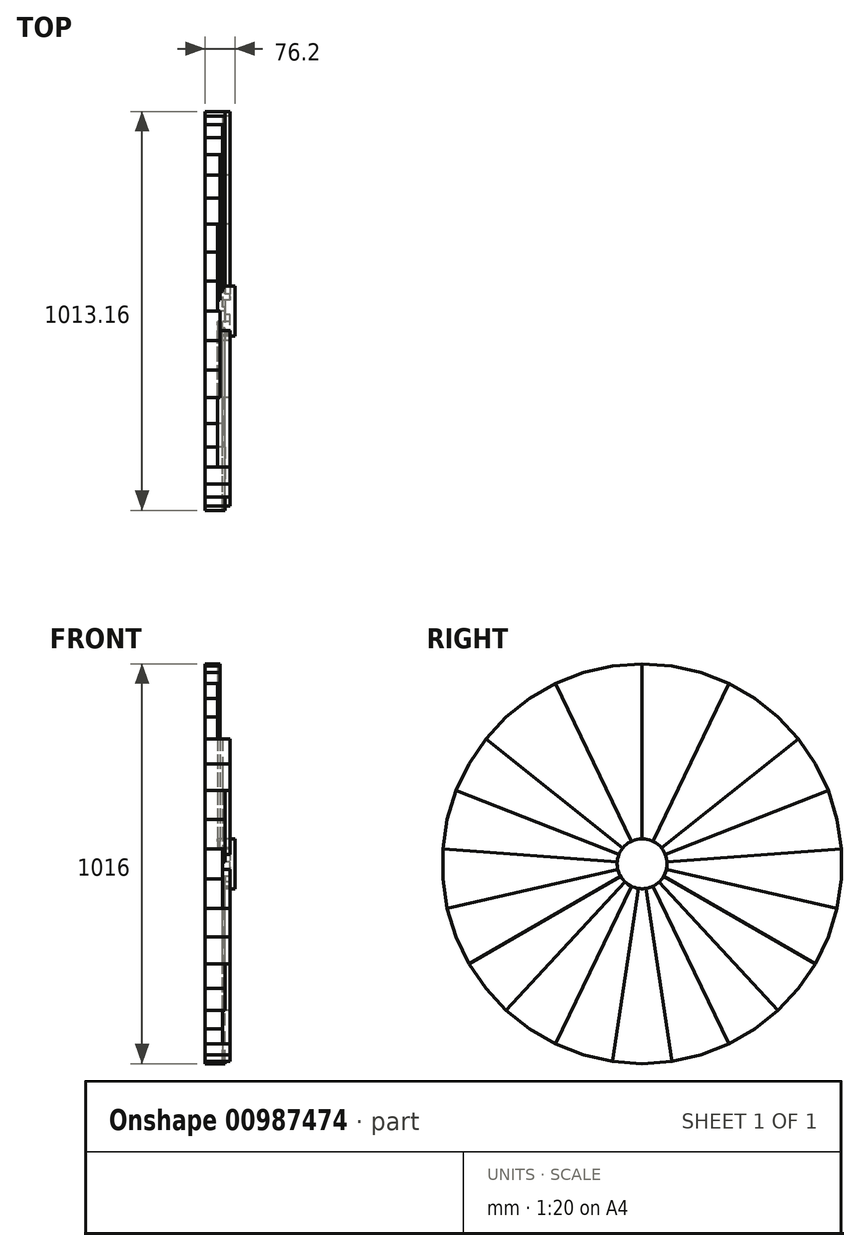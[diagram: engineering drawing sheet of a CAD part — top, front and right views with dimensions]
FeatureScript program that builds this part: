
annotation { "Feature Type Name" : "Feature", "Feature Type Description" : "" }
export const myFeature = defineFeature(function(context is Context, id is Id, definition is map)
    precondition{}
    {
        {
            var Q0;
            Q0=qCreatedBy(makeId("Right.planeOp"),FACE);
            var sketch = newSketch(context, id + "F0", { "sketchPlane" : qUnion([Q0])});
            skCircle(sketch, "E0", {"center": v(0, 0) * mm, "radius": 508 * mm});
            skCircle(sketch, "E1.cCircle", {"center": v(0, 0) * mm, "radius": 508 * mm, "construction": true});
            skLineSegment(sketch, "E1.0", {"start": v(-220.41, 457.7) * mm, "end": v(-149.74, 485.43) * mm});
            skLineSegment(sketch, "E1.1", {"start": v(-149.74, 485.43) * mm, "end": v(-75.71, 502.33) * mm});
            skLineSegment(sketch, "E1.2", {"start": v(-75.71, 502.33) * mm, "end": v(0, 508) * mm});
            skLineSegment(sketch, "E1.3", {"start": v(0, 508) * mm, "end": v(75.71, 502.33) * mm});
            skLineSegment(sketch, "E1.4", {"start": v(75.71, 502.33) * mm, "end": v(149.74, 485.43) * mm});
            skLineSegment(sketch, "E1.5", {"start": v(149.74, 485.43) * mm, "end": v(220.41, 457.7) * mm});
            skLineSegment(sketch, "E1.6", {"start": v(220.41, 457.7) * mm, "end": v(286.17, 419.73) * mm});
            skLineSegment(sketch, "E1.7", {"start": v(286.17, 419.73) * mm, "end": v(345.53, 372.4) * mm});
            skLineSegment(sketch, "E1.8", {"start": v(345.53, 372.4) * mm, "end": v(397.17, 316.73) * mm});
            skLineSegment(sketch, "E1.9", {"start": v(397.17, 316.73) * mm, "end": v(439.94, 254) * mm});
            skLineSegment(sketch, "E1.10", {"start": v(439.94, 254) * mm, "end": v(472.88, 185.6) * mm});
            skLineSegment(sketch, "E1.11", {"start": v(472.88, 185.6) * mm, "end": v(495.26, 113.04) * mm});
            skLineSegment(sketch, "E1.12", {"start": v(495.26, 113.04) * mm, "end": v(506.58, 37.96) * mm});
            skLineSegment(sketch, "E1.13", {"start": v(506.58, 37.96) * mm, "end": v(506.58, -37.96) * mm});
            skLineSegment(sketch, "E1.14", {"start": v(506.58, -37.96) * mm, "end": v(495.26, -113.04) * mm});
            skLineSegment(sketch, "E1.15", {"start": v(495.26, -113.04) * mm, "end": v(472.88, -185.6) * mm});
            skLineSegment(sketch, "E1.16", {"start": v(472.88, -185.6) * mm, "end": v(439.94, -254) * mm});
            skLineSegment(sketch, "E1.17", {"start": v(439.94, -254) * mm, "end": v(397.17, -316.73) * mm});
            skLineSegment(sketch, "E1.18", {"start": v(397.17, -316.73) * mm, "end": v(345.53, -372.4) * mm});
            skLineSegment(sketch, "E1.19", {"start": v(345.53, -372.4) * mm, "end": v(286.17, -419.73) * mm});
            skLineSegment(sketch, "E1.20", {"start": v(286.17, -419.73) * mm, "end": v(220.41, -457.7) * mm});
            skLineSegment(sketch, "E1.21", {"start": v(220.41, -457.7) * mm, "end": v(149.74, -485.43) * mm});
            skLineSegment(sketch, "E1.22", {"start": v(149.74, -485.43) * mm, "end": v(75.71, -502.33) * mm});
            skLineSegment(sketch, "E1.23", {"start": v(75.71, -502.33) * mm, "end": v(0, -508) * mm});
            skLineSegment(sketch, "E1.24", {"start": v(0, -508) * mm, "end": v(-75.71, -502.33) * mm});
            skLineSegment(sketch, "E1.25", {"start": v(-75.71, -502.33) * mm, "end": v(-149.74, -485.43) * mm});
            skLineSegment(sketch, "E1.26", {"start": v(-149.74, -485.43) * mm, "end": v(-220.41, -457.7) * mm});
            skLineSegment(sketch, "E1.27", {"start": v(-220.41, -457.7) * mm, "end": v(-286.17, -419.73) * mm});
            skLineSegment(sketch, "E1.28", {"start": v(-286.17, -419.73) * mm, "end": v(-345.53, -372.4) * mm});
            skLineSegment(sketch, "E1.29", {"start": v(-345.53, -372.4) * mm, "end": v(-397.17, -316.73) * mm});
            skLineSegment(sketch, "E1.30", {"start": v(-397.17, -316.73) * mm, "end": v(-439.94, -254) * mm});
            skLineSegment(sketch, "E1.31", {"start": v(-439.94, -254) * mm, "end": v(-472.88, -185.6) * mm});
            skLineSegment(sketch, "E1.32", {"start": v(-472.88, -185.6) * mm, "end": v(-495.26, -113.04) * mm});
            skLineSegment(sketch, "E1.33", {"start": v(-495.26, -113.04) * mm, "end": v(-506.58, -37.96) * mm});
            skLineSegment(sketch, "E1.34", {"start": v(-506.58, -37.96) * mm, "end": v(-506.58, 37.96) * mm});
            skLineSegment(sketch, "E1.35", {"start": v(-506.58, 37.96) * mm, "end": v(-495.26, 113.04) * mm});
            skLineSegment(sketch, "E1.36", {"start": v(-495.26, 113.04) * mm, "end": v(-472.88, 185.6) * mm});
            skLineSegment(sketch, "E1.37", {"start": v(-472.88, 185.6) * mm, "end": v(-439.94, 254) * mm});
            skLineSegment(sketch, "E1.38", {"start": v(-439.94, 254) * mm, "end": v(-397.17, 316.73) * mm});
            skLineSegment(sketch, "E1.39", {"start": v(-397.17, 316.73) * mm, "end": v(-345.53, 372.4) * mm});
            skLineSegment(sketch, "E1.40", {"start": v(-345.53, 372.4) * mm, "end": v(-286.17, 419.73) * mm});
            skLineSegment(sketch, "E1.41", {"start": v(-286.17, 419.73) * mm, "end": v(-220.41, 457.7) * mm});
            skLineSegment(sketch, "E2", {"start": v(0, 508) * mm, "end": v(0, 0) * mm});
            skLineSegment(sketch, "E3", {"start": v(220.41, 457.7) * mm, "end": v(0, 0) * mm});
            skLineSegment(sketch, "E4", {"start": v(397.17, 316.73) * mm, "end": v(0, 0) * mm});
            skLineSegment(sketch, "E5", {"start": v(-220.41, 457.7) * mm, "end": v(0, 0) * mm});
            skLineSegment(sketch, "E6", {"start": v(-397.17, 316.73) * mm, "end": v(0, 0) * mm});
            skLineSegment(sketch, "E7", {"start": v(472.88, 185.6) * mm, "end": v(0, 0) * mm});
            skLineSegment(sketch, "E8", {"start": v(506.58, 37.96) * mm, "end": v(0, 0) * mm});
            skLineSegment(sketch, "E9", {"start": v(495.26, -113.04) * mm, "end": v(0, 0) * mm});
            skLineSegment(sketch, "E10", {"start": v(439.94, -254) * mm, "end": v(0, 0) * mm});
            skLineSegment(sketch, "E11", {"start": v(345.53, -372.4) * mm, "end": v(0, 0) * mm});
            skLineSegment(sketch, "E12", {"start": v(220.41, -457.7) * mm, "end": v(0, 0) * mm});
            skLineSegment(sketch, "E13", {"start": v(75.71, -502.33) * mm, "end": v(0, 0) * mm});
            skLineSegment(sketch, "E14", {"start": v(-75.71, -502.33) * mm, "end": v(0, 0) * mm});
            skLineSegment(sketch, "E15", {"start": v(-220.41, -457.7) * mm, "end": v(0, 0) * mm});
            skLineSegment(sketch, "E16", {"start": v(-345.53, -372.4) * mm, "end": v(0, 0) * mm});
            skLineSegment(sketch, "E17", {"start": v(-439.94, -254) * mm, "end": v(0, 0) * mm});
            skLineSegment(sketch, "E18", {"start": v(-495.26, -113.04) * mm, "end": v(0, 0) * mm});
            skLineSegment(sketch, "E19", {"start": v(-506.58, 37.96) * mm, "end": v(0, 0) * mm});
            skLineSegment(sketch, "E20", {"start": v(-472.88, 185.6) * mm, "end": v(0, 0) * mm});
            skCircle(sketch, "E21", {"center": v(1271.03, -28.32) * mm, "radius": 508 * mm});
            skCircle(sketch, "E22", {"center": v(-1617.24, 20.06) * mm, "radius": 508 * mm});
            skCircle(sketch, "E23.cCircle", {"center": v(-1617.24, 20.06) * mm, "radius": 508 * mm, "construction": true});
            skLineSegment(sketch, "E23.0", {"start": v(-1897.2, 443.96) * mm, "end": v(-1830.9, 480.95) * mm});
            skLineSegment(sketch, "E23.1", {"start": v(-1830.9, 480.95) * mm, "end": v(-1759.81, 507.65) * mm});
            skLineSegment(sketch, "E23.2", {"start": v(-1759.81, 507.65) * mm, "end": v(-1685.55, 523.45) * mm});
            skLineSegment(sketch, "E23.3", {"start": v(-1685.55, 523.45) * mm, "end": v(-1609.76, 528) * mm});
            skLineSegment(sketch, "E23.4", {"start": v(-1609.76, 528) * mm, "end": v(-1534.14, 521.22) * mm});
            skLineSegment(sketch, "E23.5", {"start": v(-1534.14, 521.22) * mm, "end": v(-1460.37, 503.23) * mm});
            skLineSegment(sketch, "E23.6", {"start": v(-1460.37, 503.23) * mm, "end": v(-1390.11, 474.46) * mm});
            skLineSegment(sketch, "E23.7", {"start": v(-1390.11, 474.46) * mm, "end": v(-1324.93, 435.53) * mm});
            skLineSegment(sketch, "E23.8", {"start": v(-1324.93, 435.53) * mm, "end": v(-1266.27, 387.32) * mm});
            skLineSegment(sketch, "E23.9", {"start": v(-1266.27, 387.32) * mm, "end": v(-1215.45, 330.9) * mm});
            skLineSegment(sketch, "E23.10", {"start": v(-1215.45, 330.9) * mm, "end": v(-1173.6, 267.55) * mm});
            skLineSegment(sketch, "E23.11", {"start": v(-1173.6, 267.55) * mm, "end": v(-1141.68, 198.67) * mm});
            skLineSegment(sketch, "E23.12", {"start": v(-1141.68, 198.67) * mm, "end": v(-1120.37, 125.8) * mm});
            skLineSegment(sketch, "E23.13", {"start": v(-1120.37, 125.8) * mm, "end": v(-1110.16, 50.56) * mm});
            skLineSegment(sketch, "E23.14", {"start": v(-1110.16, 50.56) * mm, "end": v(-1111.28, -25.36) * mm});
            skLineSegment(sketch, "E23.15", {"start": v(-1111.28, -25.36) * mm, "end": v(-1123.7, -100.26) * mm});
            skLineSegment(sketch, "E23.16", {"start": v(-1123.7, -100.26) * mm, "end": v(-1147.15, -172.48) * mm});
            skLineSegment(sketch, "E23.17", {"start": v(-1147.15, -172.48) * mm, "end": v(-1181.1, -240.4) * mm});
            skLineSegment(sketch, "E23.18", {"start": v(-1181.1, -240.4) * mm, "end": v(-1224.78, -302.49) * mm});
            skLineSegment(sketch, "E23.19", {"start": v(-1224.78, -302.49) * mm, "end": v(-1277.24, -357.38) * mm});
            skLineSegment(sketch, "E23.20", {"start": v(-1277.24, -357.38) * mm, "end": v(-1337.3, -403.84) * mm});
            skLineSegment(sketch, "E23.21", {"start": v(-1337.3, -403.84) * mm, "end": v(-1403.6, -440.83) * mm});
            skLineSegment(sketch, "E23.22", {"start": v(-1403.6, -440.83) * mm, "end": v(-1474.68, -467.52) * mm});
            skLineSegment(sketch, "E23.23", {"start": v(-1474.68, -467.52) * mm, "end": v(-1548.94, -483.33) * mm});
            skLineSegment(sketch, "E23.24", {"start": v(-1548.94, -483.33) * mm, "end": v(-1624.73, -487.88) * mm});
            skLineSegment(sketch, "E23.25", {"start": v(-1624.73, -487.88) * mm, "end": v(-1700.35, -481.1) * mm});
            skLineSegment(sketch, "E23.26", {"start": v(-1700.35, -481.1) * mm, "end": v(-1774.11, -463.11) * mm});
            skLineSegment(sketch, "E23.27", {"start": v(-1774.11, -463.11) * mm, "end": v(-1844.38, -434.33) * mm});
            skLineSegment(sketch, "E23.28", {"start": v(-1844.38, -434.33) * mm, "end": v(-1909.56, -395.4) * mm});
            skLineSegment(sketch, "E23.29", {"start": v(-1909.56, -395.4) * mm, "end": v(-1968.22, -347.2) * mm});
            skLineSegment(sketch, "E23.30", {"start": v(-1968.22, -347.2) * mm, "end": v(-2019.04, -290.79) * mm});
            skLineSegment(sketch, "E23.31", {"start": v(-2019.04, -290.79) * mm, "end": v(-2060.88, -227.43) * mm});
            skLineSegment(sketch, "E23.32", {"start": v(-2060.88, -227.43) * mm, "end": v(-2092.81, -158.55) * mm});
            skLineSegment(sketch, "E23.33", {"start": v(-2092.81, -158.55) * mm, "end": v(-2114.12, -85.67) * mm});
            skLineSegment(sketch, "E23.34", {"start": v(-2114.12, -85.67) * mm, "end": v(-2124.33, -10.43) * mm});
            skLineSegment(sketch, "E23.35", {"start": v(-2124.33, -10.43) * mm, "end": v(-2123.2, 65.48) * mm});
            skLineSegment(sketch, "E23.36", {"start": v(-2123.2, 65.48) * mm, "end": v(-2110.79, 140.39) * mm});
            skLineSegment(sketch, "E23.37", {"start": v(-2110.79, 140.39) * mm, "end": v(-2087.34, 212.6) * mm});
            skLineSegment(sketch, "E23.38", {"start": v(-2087.34, 212.6) * mm, "end": v(-2053.4, 280.51) * mm});
            skLineSegment(sketch, "E23.39", {"start": v(-2053.4, 280.51) * mm, "end": v(-2009.7, 342.61) * mm});
            skLineSegment(sketch, "E23.40", {"start": v(-2009.7, 342.61) * mm, "end": v(-1957.25, 397.5) * mm});
            skLineSegment(sketch, "E23.41", {"start": v(-1957.25, 397.5) * mm, "end": v(-1897.2, 443.96) * mm});
            skLineSegment(sketch, "E24", {"start": v(-1685.55, 523.45) * mm, "end": v(-1617.24, 20.06) * mm});
            skLineSegment(sketch, "E25", {"start": v(-1460.37, 503.23) * mm, "end": v(-1617.24, 20.06) * mm});
            skLineSegment(sketch, "E26", {"start": v(-1266.27, 387.32) * mm, "end": v(-1617.24, 20.06) * mm});
            skLineSegment(sketch, "E27", {"start": v(-1897.2, 443.96) * mm, "end": v(-1617.24, 20.06) * mm});
            skLineSegment(sketch, "E28", {"start": v(-2053.4, 280.51) * mm, "end": v(-1617.24, 20.06) * mm});
            skLineSegment(sketch, "E29", {"start": v(-1173.6, 267.55) * mm, "end": v(-1617.24, 20.06) * mm});
            skLineSegment(sketch, "E30", {"start": v(-1120.37, 125.8) * mm, "end": v(-1617.24, 20.06) * mm});
            skLineSegment(sketch, "E31", {"start": v(-1111.28, -25.36) * mm, "end": v(-1617.24, 20.06) * mm});
            skLineSegment(sketch, "E32", {"start": v(-1147.15, -172.48) * mm, "end": v(-1617.24, 20.06) * mm});
            skLineSegment(sketch, "E33", {"start": v(-1224.78, -302.49) * mm, "end": v(-1617.24, 20.06) * mm});
            skLineSegment(sketch, "E34", {"start": v(-1337.3, -403.84) * mm, "end": v(-1617.24, 20.06) * mm});
            skLineSegment(sketch, "E35", {"start": v(-1474.68, -467.52) * mm, "end": v(-1617.24, 20.06) * mm});
            skLineSegment(sketch, "E36", {"start": v(-1624.73, -487.88) * mm, "end": v(-1617.24, 20.06) * mm});
            skLineSegment(sketch, "E37", {"start": v(-1774.11, -463.11) * mm, "end": v(-1617.24, 20.06) * mm});
            skLineSegment(sketch, "E38", {"start": v(-1909.56, -395.4) * mm, "end": v(-1617.24, 20.06) * mm});
            skLineSegment(sketch, "E39", {"start": v(-2019.04, -290.79) * mm, "end": v(-1617.24, 20.06) * mm});
            skLineSegment(sketch, "E40", {"start": v(-2092.81, -158.55) * mm, "end": v(-1617.24, 20.06) * mm});
            skLineSegment(sketch, "E41", {"start": v(-2124.33, -10.43) * mm, "end": v(-1617.24, 20.06) * mm});
            skLineSegment(sketch, "E42", {"start": v(-2110.79, 140.39) * mm, "end": v(-1617.24, 20.06) * mm});
            skCircle(sketch, "E43", {"center": v(0, 0) * mm, "radius": 63.5 * mm});
            skSolve(sketch);
        }
        {
            var Q0;
            Q0=makeQuery(id+"F0.imprint","IMPRINT",FACE,{"disambiguationData":[TD([[makeQuery(id+"F0.imprint","IMPRINT",EDGE,{"derivedFrom":sQuery(id+"F0.wireOp",EDGE,"E1.0")}),-1.0]])]});
            var Q1;
            Q1=makeQuery(id+"F0.imprint","IMPRINT",FACE,{"disambiguationData":[TD([[makeQuery(id+"F0.imprint","IMPRINT",EDGE,{"derivedFrom":sQuery(id+"F0.wireOp",EDGE,"E1.3")}),-1.0]])]});
            var Q2;
            Q2=makeQuery(id+"F0.imprint","IMPRINT",FACE,{"disambiguationData":[TD([[makeQuery(id+"F0.imprint","IMPRINT",EDGE,{"derivedFrom":sQuery(id+"F0.wireOp",EDGE,"E1.6")}),-1.0]])]});
            var Q3;
            Q3=makeQuery(id+"F0.imprint","IMPRINT",FACE,{"disambiguationData":[TD([[makeQuery(id+"F0.imprint","IMPRINT",EDGE,{"derivedFrom":sQuery(id+"F0.wireOp",EDGE,"E1.9")}),-1.0]])]});
            var Q4;
            Q4=makeQuery(id+"F0.imprint","IMPRINT",FACE,{"disambiguationData":[TD([[makeQuery(id+"F0.imprint","IMPRINT",EDGE,{"derivedFrom":sQuery(id+"F0.wireOp",EDGE,"E1.11")}),-1.0]])]});
            var Q5;
            Q5=makeQuery(id+"F0.imprint","IMPRINT",FACE,{"disambiguationData":[TD([[makeQuery(id+"F0.imprint","IMPRINT",EDGE,{"derivedFrom":sQuery(id+"F0.wireOp",EDGE,"E1.13")}),-1.0]])]});
            var Q6;
            Q6=makeQuery(id+"F0.imprint","IMPRINT",FACE,{"disambiguationData":[TD([[makeQuery(id+"F0.imprint","IMPRINT",EDGE,{"derivedFrom":sQuery(id+"F0.wireOp",EDGE,"E1.15")}),-1.0]])]});
            var Q7;
            Q7=makeQuery(id+"F0.imprint","IMPRINT",FACE,{"disambiguationData":[TD([[makeQuery(id+"F0.imprint","IMPRINT",EDGE,{"derivedFrom":sQuery(id+"F0.wireOp",EDGE,"E1.17")}),-1.0]])]});
            var Q8;
            Q8=makeQuery(id+"F0.imprint","IMPRINT",FACE,{"disambiguationData":[TD([[makeQuery(id+"F0.imprint","IMPRINT",EDGE,{"derivedFrom":sQuery(id+"F0.wireOp",EDGE,"E1.19")}),-1.0]])]});
            var Q9;
            Q9=makeQuery(id+"F0.imprint","IMPRINT",FACE,{"disambiguationData":[TD([[makeQuery(id+"F0.imprint","IMPRINT",EDGE,{"derivedFrom":sQuery(id+"F0.wireOp",EDGE,"E1.21")}),-1.0]])]});
            var Q10;
            Q10=makeQuery(id+"F0.imprint","IMPRINT",FACE,{"disambiguationData":[TD([[makeQuery(id+"F0.imprint","IMPRINT",EDGE,{"derivedFrom":sQuery(id+"F0.wireOp",EDGE,"E1.23")}),-1.0]])]});
            var Q11;
            Q11=makeQuery(id+"F0.imprint","IMPRINT",FACE,{"disambiguationData":[TD([[makeQuery(id+"F0.imprint","IMPRINT",EDGE,{"derivedFrom":sQuery(id+"F0.wireOp",EDGE,"E1.25")}),-1.0]])]});
            var Q12;
            Q12=makeQuery(id+"F0.imprint","IMPRINT",FACE,{"disambiguationData":[TD([[makeQuery(id+"F0.imprint","IMPRINT",EDGE,{"derivedFrom":sQuery(id+"F0.wireOp",EDGE,"E1.27")}),-1.0]])]});
            var Q13;
            Q13=makeQuery(id+"F0.imprint","IMPRINT",FACE,{"disambiguationData":[TD([[makeQuery(id+"F0.imprint","IMPRINT",EDGE,{"derivedFrom":sQuery(id+"F0.wireOp",EDGE,"E1.29")}),-1.0]])]});
            var Q14;
            Q14=makeQuery(id+"F0.imprint","IMPRINT",FACE,{"disambiguationData":[TD([[makeQuery(id+"F0.imprint","IMPRINT",EDGE,{"derivedFrom":sQuery(id+"F0.wireOp",EDGE,"E1.31")}),-1.0]])]});
            var Q15;
            Q15=makeQuery(id+"F0.imprint","IMPRINT",FACE,{"disambiguationData":[TD([[makeQuery(id+"F0.imprint","IMPRINT",EDGE,{"derivedFrom":sQuery(id+"F0.wireOp",EDGE,"E1.33")}),-1.0]])]});
            var Q16;
            Q16=makeQuery(id+"F0.imprint","IMPRINT",FACE,{"disambiguationData":[TD([[makeQuery(id+"F0.imprint","IMPRINT",EDGE,{"derivedFrom":sQuery(id+"F0.wireOp",EDGE,"E1.35")}),-1.0]])]});
            var Q17;
            Q17=makeQuery(id+"F0.imprint","IMPRINT",FACE,{"disambiguationData":[TD([[makeQuery(id+"F0.imprint","IMPRINT",EDGE,{"derivedFrom":sQuery(id+"F0.wireOp",EDGE,"E1.37")}),-1.0]])]});
            var Q18;
            Q18=makeQuery(id+"F0.imprint","IMPRINT",FACE,{"disambiguationData":[TD([[makeQuery(id+"F0.imprint","IMPRINT",EDGE,{"derivedFrom":sQuery(id+"F0.wireOp",EDGE,"E1.39")}),-1.0]])]});
            extrude(context, id + "F1", {"entities" : qUnion([Q0, Q1, Q2, Q3, Q4, Q5, Q6, Q7, Q8, Q9, Q10, Q11, Q12, Q13, Q14, Q15, Q16, Q17, Q18]), "depth" : 25.4 * mm, "offsetDistance" : 25.4 * mm});
        }
        {
            var Q0;
            {var subQ1=sQuery(id+"F0.wireOp",EDGE,"E1.3");Q0=makeQuery(id+"F0.imprint","IMPRINT",FACE,{"disambiguationData":[TD([[makeQuery(id+"F0.imprint","IMPRINT",EDGE,{"derivedFrom":subQ1}),-1.0]])]});}
            var Q1;
            {var subQ5=sQuery(id+"F0.wireOp",EDGE,"E1.39");Q1=makeQuery(id+"F0.imprint","IMPRINT",FACE,{"disambiguationData":[TD([[makeQuery(id+"F0.imprint","IMPRINT",EDGE,{"derivedFrom":subQ5}),-1.0]])]});}
            var Q2;
            {var subQ1=sQuery(id+"F0.wireOp",EDGE,"E2");var subQ3=sQuery(id+"F0.wireOp",EDGE,"E43");var subQ4=makeQuery(id+"F0.imprint","INTERSECT",VERTEX,{"derivedFrom":[subQ1,subQ3]});Q2=makeQuery(id+"F0.imprint","IMPRINT",FACE,{"disambiguationData":[TD([[makeQuery(id+"F0.imprint","IMPRINT",EDGE,{"disambiguationData":[TD([[subQ4,1.0]])],"derivedFrom":subQ3}),1.0]])]});}
            var Q3;
            {var subQ1=sQuery(id+"F0.wireOp",EDGE,"E2");var subQ3=sQuery(id+"F0.wireOp",EDGE,"E43");var subQ4=makeQuery(id+"F0.imprint","INTERSECT",VERTEX,{"derivedFrom":[subQ1,subQ3]});Q3=makeQuery(id+"F0.imprint","IMPRINT",FACE,{"disambiguationData":[TD([[makeQuery(id+"F0.imprint","IMPRINT",EDGE,{"disambiguationData":[TD([[subQ4,-1.0]])],"derivedFrom":subQ3}),1.0]])]});}
            var Q4;
            {var subQ1=sQuery(id+"F0.wireOp",EDGE,"E5");var subQ3=sQuery(id+"F0.wireOp",EDGE,"E43");var subQ4=makeQuery(id+"F0.imprint","INTERSECT",VERTEX,{"derivedFrom":[subQ1,subQ3]});Q4=makeQuery(id+"F0.imprint","IMPRINT",FACE,{"disambiguationData":[TD([[makeQuery(id+"F0.imprint","IMPRINT",EDGE,{"disambiguationData":[TD([[subQ4,-1.0]])],"derivedFrom":subQ3}),1.0]])]});}
            extrude(context, id + "F2", {"entities" : qUnion([Q0, Q1, Q2, Q3, Q4]), "operationType" : NewBodyOperationType.ADD, "depth" : 31.75 * mm, "offsetDistance" : 25.4 * mm});
        }
        {
            var Q0;
            {var subQ7=sQuery(id+"F0.wireOp",EDGE,"E1.0");Q0=makeQuery(id+"F0.imprint","IMPRINT",FACE,{"disambiguationData":[TD([[makeQuery(id+"F0.imprint","IMPRINT",EDGE,{"derivedFrom":subQ7}),-1.0]])]});}
            var Q1;
            {var subQ1=sQuery(id+"F0.wireOp",EDGE,"E1.6");Q1=makeQuery(id+"F0.imprint","IMPRINT",FACE,{"disambiguationData":[TD([[makeQuery(id+"F0.imprint","IMPRINT",EDGE,{"derivedFrom":subQ1}),-1.0]])]});}
            var Q2;
            {var subQ1=sQuery(id+"F0.wireOp",EDGE,"E3");var subQ3=sQuery(id+"F0.wireOp",EDGE,"E43");var subQ4=makeQuery(id+"F0.imprint","INTERSECT",VERTEX,{"derivedFrom":[subQ1,subQ3]});Q2=makeQuery(id+"F0.imprint","IMPRINT",FACE,{"disambiguationData":[TD([[makeQuery(id+"F0.imprint","IMPRINT",EDGE,{"disambiguationData":[TD([[subQ4,1.0]])],"derivedFrom":subQ3}),1.0]])]});}
            var Q3;
            {var subQ1=sQuery(id+"F0.wireOp",EDGE,"E2");var subQ3=sQuery(id+"F0.wireOp",EDGE,"E43");var subQ4=makeQuery(id+"F0.imprint","INTERSECT",VERTEX,{"derivedFrom":[subQ1,subQ3]});Q3=makeQuery(id+"F0.imprint","IMPRINT",FACE,{"disambiguationData":[TD([[makeQuery(id+"F0.imprint","IMPRINT",EDGE,{"disambiguationData":[TD([[subQ4,1.0]])],"derivedFrom":subQ3}),1.0]])]});}
            var Q4;
            {var subQ1=sQuery(id+"F0.wireOp",EDGE,"E2");var subQ3=sQuery(id+"F0.wireOp",EDGE,"E43");var subQ4=makeQuery(id+"F0.imprint","INTERSECT",VERTEX,{"derivedFrom":[subQ1,subQ3]});Q4=makeQuery(id+"F0.imprint","IMPRINT",FACE,{"disambiguationData":[TD([[makeQuery(id+"F0.imprint","IMPRINT",EDGE,{"disambiguationData":[TD([[subQ4,-1.0]])],"derivedFrom":subQ3}),1.0]])]});}
            extrude(context, id + "F3", {"entities" : qUnion([Q0, Q1, Q2, Q3, Q4]), "operationType" : NewBodyOperationType.ADD, "depth" : 38.1 * mm, "offsetDistance" : 25.4 * mm});
        }
        {
            var Q0;
            {var subQ6=sQuery(id+"F0.wireOp",EDGE,"E1.9");Q0=makeQuery(id+"F0.imprint","IMPRINT",FACE,{"disambiguationData":[TD([[makeQuery(id+"F0.imprint","IMPRINT",EDGE,{"derivedFrom":subQ6}),-1.0]])]});}
            var Q1;
            {var subQ7=sQuery(id+"F0.wireOp",EDGE,"E1.15");Q1=makeQuery(id+"F0.imprint","IMPRINT",FACE,{"disambiguationData":[TD([[makeQuery(id+"F0.imprint","IMPRINT",EDGE,{"derivedFrom":subQ7}),-1.0]])]});}
            var Q2;
            {var subQ6=sQuery(id+"F0.wireOp",EDGE,"E1.21");Q2=makeQuery(id+"F0.imprint","IMPRINT",FACE,{"disambiguationData":[TD([[makeQuery(id+"F0.imprint","IMPRINT",EDGE,{"derivedFrom":subQ6}),-1.0]])]});}
            var Q3;
            {var subQ6=sQuery(id+"F0.wireOp",EDGE,"E1.27");Q3=makeQuery(id+"F0.imprint","IMPRINT",FACE,{"disambiguationData":[TD([[makeQuery(id+"F0.imprint","IMPRINT",EDGE,{"derivedFrom":subQ6}),-1.0]])]});}
            var Q4;
            {var subQ6=sQuery(id+"F0.wireOp",EDGE,"E1.33");Q4=makeQuery(id+"F0.imprint","IMPRINT",FACE,{"disambiguationData":[TD([[makeQuery(id+"F0.imprint","IMPRINT",EDGE,{"derivedFrom":subQ6}),-1.0]])]});}
            var Q5;
            {var subQ1=sQuery(id+"F0.wireOp",EDGE,"E4");var subQ3=sQuery(id+"F0.wireOp",EDGE,"E43");var subQ4=makeQuery(id+"F0.imprint","INTERSECT",VERTEX,{"derivedFrom":[subQ1,subQ3]});Q5=makeQuery(id+"F0.imprint","IMPRINT",FACE,{"disambiguationData":[TD([[makeQuery(id+"F0.imprint","IMPRINT",EDGE,{"disambiguationData":[TD([[subQ4,1.0]])],"derivedFrom":subQ3}),1.0]])]});}
            var Q6;
            {var subQ1=sQuery(id+"F0.wireOp",EDGE,"E7");var subQ3=sQuery(id+"F0.wireOp",EDGE,"E43");var subQ4=makeQuery(id+"F0.imprint","INTERSECT",VERTEX,{"derivedFrom":[subQ1,subQ3]});Q6=makeQuery(id+"F0.imprint","IMPRINT",FACE,{"disambiguationData":[TD([[makeQuery(id+"F0.imprint","IMPRINT",EDGE,{"disambiguationData":[TD([[subQ4,1.0]])],"derivedFrom":subQ3}),1.0]])]});}
            var Q7;
            {var subQ1=sQuery(id+"F0.wireOp",EDGE,"E8");var subQ3=sQuery(id+"F0.wireOp",EDGE,"E43");var subQ4=makeQuery(id+"F0.imprint","INTERSECT",VERTEX,{"derivedFrom":[subQ1,subQ3]});Q7=makeQuery(id+"F0.imprint","IMPRINT",FACE,{"disambiguationData":[TD([[makeQuery(id+"F0.imprint","IMPRINT",EDGE,{"disambiguationData":[TD([[subQ4,1.0]])],"derivedFrom":subQ3}),1.0]])]});}
            var Q8;
            {var subQ1=sQuery(id+"F0.wireOp",EDGE,"E9");var subQ3=sQuery(id+"F0.wireOp",EDGE,"E43");var subQ4=makeQuery(id+"F0.imprint","INTERSECT",VERTEX,{"derivedFrom":[subQ1,subQ3]});Q8=makeQuery(id+"F0.imprint","IMPRINT",FACE,{"disambiguationData":[TD([[makeQuery(id+"F0.imprint","IMPRINT",EDGE,{"disambiguationData":[TD([[subQ4,1.0]])],"derivedFrom":subQ3}),1.0]])]});}
            var Q9;
            {var subQ1=sQuery(id+"F0.wireOp",EDGE,"E10");var subQ3=sQuery(id+"F0.wireOp",EDGE,"E43");var subQ4=makeQuery(id+"F0.imprint","INTERSECT",VERTEX,{"derivedFrom":[subQ1,subQ3]});Q9=makeQuery(id+"F0.imprint","IMPRINT",FACE,{"disambiguationData":[TD([[makeQuery(id+"F0.imprint","IMPRINT",EDGE,{"disambiguationData":[TD([[subQ4,1.0]])],"derivedFrom":subQ3}),1.0]])]});}
            var Q10;
            {var subQ1=sQuery(id+"F0.wireOp",EDGE,"E11");var subQ3=sQuery(id+"F0.wireOp",EDGE,"E43");var subQ4=makeQuery(id+"F0.imprint","INTERSECT",VERTEX,{"derivedFrom":[subQ1,subQ3]});Q10=makeQuery(id+"F0.imprint","IMPRINT",FACE,{"disambiguationData":[TD([[makeQuery(id+"F0.imprint","IMPRINT",EDGE,{"disambiguationData":[TD([[subQ4,1.0]])],"derivedFrom":subQ3}),1.0]])]});}
            var Q11;
            {var subQ1=sQuery(id+"F0.wireOp",EDGE,"E12");var subQ3=sQuery(id+"F0.wireOp",EDGE,"E43");var subQ4=makeQuery(id+"F0.imprint","INTERSECT",VERTEX,{"derivedFrom":[subQ1,subQ3]});Q11=makeQuery(id+"F0.imprint","IMPRINT",FACE,{"disambiguationData":[TD([[makeQuery(id+"F0.imprint","IMPRINT",EDGE,{"disambiguationData":[TD([[subQ4,1.0]])],"derivedFrom":subQ3}),1.0]])]});}
            var Q12;
            {var subQ1=sQuery(id+"F0.wireOp",EDGE,"E13");var subQ3=sQuery(id+"F0.wireOp",EDGE,"E43");var subQ4=makeQuery(id+"F0.imprint","INTERSECT",VERTEX,{"derivedFrom":[subQ1,subQ3]});Q12=makeQuery(id+"F0.imprint","IMPRINT",FACE,{"disambiguationData":[TD([[makeQuery(id+"F0.imprint","IMPRINT",EDGE,{"disambiguationData":[TD([[subQ4,1.0]])],"derivedFrom":subQ3}),1.0]])]});}
            var Q13;
            {var subQ1=sQuery(id+"F0.wireOp",EDGE,"E14");var subQ3=sQuery(id+"F0.wireOp",EDGE,"E43");var subQ4=makeQuery(id+"F0.imprint","INTERSECT",VERTEX,{"derivedFrom":[subQ1,subQ3]});Q13=makeQuery(id+"F0.imprint","IMPRINT",FACE,{"disambiguationData":[TD([[makeQuery(id+"F0.imprint","IMPRINT",EDGE,{"disambiguationData":[TD([[subQ4,1.0]])],"derivedFrom":subQ3}),1.0]])]});}
            var Q14;
            {var subQ1=sQuery(id+"F0.wireOp",EDGE,"E15");var subQ3=sQuery(id+"F0.wireOp",EDGE,"E43");var subQ4=makeQuery(id+"F0.imprint","INTERSECT",VERTEX,{"derivedFrom":[subQ1,subQ3]});Q14=makeQuery(id+"F0.imprint","IMPRINT",FACE,{"disambiguationData":[TD([[makeQuery(id+"F0.imprint","IMPRINT",EDGE,{"disambiguationData":[TD([[subQ4,1.0]])],"derivedFrom":subQ3}),1.0]])]});}
            var Q15;
            {var subQ1=sQuery(id+"F0.wireOp",EDGE,"E16");var subQ3=sQuery(id+"F0.wireOp",EDGE,"E43");var subQ4=makeQuery(id+"F0.imprint","INTERSECT",VERTEX,{"derivedFrom":[subQ1,subQ3]});Q15=makeQuery(id+"F0.imprint","IMPRINT",FACE,{"disambiguationData":[TD([[makeQuery(id+"F0.imprint","IMPRINT",EDGE,{"disambiguationData":[TD([[subQ4,1.0]])],"derivedFrom":subQ3}),1.0]])]});}
            var Q16;
            {var subQ1=sQuery(id+"F0.wireOp",EDGE,"E17");var subQ3=sQuery(id+"F0.wireOp",EDGE,"E43");var subQ4=makeQuery(id+"F0.imprint","INTERSECT",VERTEX,{"derivedFrom":[subQ1,subQ3]});Q16=makeQuery(id+"F0.imprint","IMPRINT",FACE,{"disambiguationData":[TD([[makeQuery(id+"F0.imprint","IMPRINT",EDGE,{"disambiguationData":[TD([[subQ4,1.0]])],"derivedFrom":subQ3}),1.0]])]});}
            var Q17;
            {var subQ1=sQuery(id+"F0.wireOp",EDGE,"E18");var subQ3=sQuery(id+"F0.wireOp",EDGE,"E43");var subQ4=makeQuery(id+"F0.imprint","INTERSECT",VERTEX,{"derivedFrom":[subQ1,subQ3]});Q17=makeQuery(id+"F0.imprint","IMPRINT",FACE,{"disambiguationData":[TD([[makeQuery(id+"F0.imprint","IMPRINT",EDGE,{"disambiguationData":[TD([[subQ4,1.0]])],"derivedFrom":subQ3}),1.0]])]});}
            extrude(context, id + "F4", {"entities" : qUnion([Q0, Q1, Q2, Q3, Q4, Q5, Q6, Q7, Q8, Q9, Q10, Q11, Q12, Q13, Q14, Q15, Q16, Q17]), "operationType" : NewBodyOperationType.ADD, "depth" : 44.45 * mm, "offsetDistance" : 25.4 * mm});
        }
        {
            var Q0;
            {var subQ6=sQuery(id+"F0.wireOp",EDGE,"E1.11");Q0=makeQuery(id+"F0.imprint","IMPRINT",FACE,{"disambiguationData":[TD([[makeQuery(id+"F0.imprint","IMPRINT",EDGE,{"derivedFrom":subQ6}),-1.0]])]});}
            var Q1;
            {var subQ6=sQuery(id+"F0.wireOp",EDGE,"E1.17");Q1=makeQuery(id+"F0.imprint","IMPRINT",FACE,{"disambiguationData":[TD([[makeQuery(id+"F0.imprint","IMPRINT",EDGE,{"derivedFrom":subQ6}),-1.0]])]});}
            var Q2;
            {var subQ6=sQuery(id+"F0.wireOp",EDGE,"E1.23");Q2=makeQuery(id+"F0.imprint","IMPRINT",FACE,{"disambiguationData":[TD([[makeQuery(id+"F0.imprint","IMPRINT",EDGE,{"derivedFrom":subQ6}),-1.0]])]});}
            var Q3;
            {var subQ6=sQuery(id+"F0.wireOp",EDGE,"E1.29");Q3=makeQuery(id+"F0.imprint","IMPRINT",FACE,{"disambiguationData":[TD([[makeQuery(id+"F0.imprint","IMPRINT",EDGE,{"derivedFrom":subQ6}),-1.0]])]});}
            var Q4;
            {var subQ6=sQuery(id+"F0.wireOp",EDGE,"E1.35");Q4=makeQuery(id+"F0.imprint","IMPRINT",FACE,{"disambiguationData":[TD([[makeQuery(id+"F0.imprint","IMPRINT",EDGE,{"derivedFrom":subQ6}),-1.0]])]});}
            var Q5;
            {var subQ1=sQuery(id+"F0.wireOp",EDGE,"E7");var subQ3=sQuery(id+"F0.wireOp",EDGE,"E43");var subQ4=makeQuery(id+"F0.imprint","INTERSECT",VERTEX,{"derivedFrom":[subQ1,subQ3]});Q5=makeQuery(id+"F0.imprint","IMPRINT",FACE,{"disambiguationData":[TD([[makeQuery(id+"F0.imprint","IMPRINT",EDGE,{"disambiguationData":[TD([[subQ4,1.0]])],"derivedFrom":subQ3}),1.0]])]});}
            var Q6;
            {var subQ1=sQuery(id+"F0.wireOp",EDGE,"E8");var subQ3=sQuery(id+"F0.wireOp",EDGE,"E43");var subQ4=makeQuery(id+"F0.imprint","INTERSECT",VERTEX,{"derivedFrom":[subQ1,subQ3]});Q6=makeQuery(id+"F0.imprint","IMPRINT",FACE,{"disambiguationData":[TD([[makeQuery(id+"F0.imprint","IMPRINT",EDGE,{"disambiguationData":[TD([[subQ4,1.0]])],"derivedFrom":subQ3}),1.0]])]});}
            var Q7;
            {var subQ1=sQuery(id+"F0.wireOp",EDGE,"E9");var subQ3=sQuery(id+"F0.wireOp",EDGE,"E43");var subQ4=makeQuery(id+"F0.imprint","INTERSECT",VERTEX,{"derivedFrom":[subQ1,subQ3]});Q7=makeQuery(id+"F0.imprint","IMPRINT",FACE,{"disambiguationData":[TD([[makeQuery(id+"F0.imprint","IMPRINT",EDGE,{"disambiguationData":[TD([[subQ4,1.0]])],"derivedFrom":subQ3}),1.0]])]});}
            var Q8;
            {var subQ1=sQuery(id+"F0.wireOp",EDGE,"E10");var subQ3=sQuery(id+"F0.wireOp",EDGE,"E43");var subQ4=makeQuery(id+"F0.imprint","INTERSECT",VERTEX,{"derivedFrom":[subQ1,subQ3]});Q8=makeQuery(id+"F0.imprint","IMPRINT",FACE,{"disambiguationData":[TD([[makeQuery(id+"F0.imprint","IMPRINT",EDGE,{"disambiguationData":[TD([[subQ4,1.0]])],"derivedFrom":subQ3}),1.0]])]});}
            var Q9;
            {var subQ1=sQuery(id+"F0.wireOp",EDGE,"E11");var subQ3=sQuery(id+"F0.wireOp",EDGE,"E43");var subQ4=makeQuery(id+"F0.imprint","INTERSECT",VERTEX,{"derivedFrom":[subQ1,subQ3]});Q9=makeQuery(id+"F0.imprint","IMPRINT",FACE,{"disambiguationData":[TD([[makeQuery(id+"F0.imprint","IMPRINT",EDGE,{"disambiguationData":[TD([[subQ4,1.0]])],"derivedFrom":subQ3}),1.0]])]});}
            var Q10;
            {var subQ1=sQuery(id+"F0.wireOp",EDGE,"E12");var subQ3=sQuery(id+"F0.wireOp",EDGE,"E43");var subQ4=makeQuery(id+"F0.imprint","INTERSECT",VERTEX,{"derivedFrom":[subQ1,subQ3]});Q10=makeQuery(id+"F0.imprint","IMPRINT",FACE,{"disambiguationData":[TD([[makeQuery(id+"F0.imprint","IMPRINT",EDGE,{"disambiguationData":[TD([[subQ4,1.0]])],"derivedFrom":subQ3}),1.0]])]});}
            var Q11;
            {var subQ1=sQuery(id+"F0.wireOp",EDGE,"E13");var subQ3=sQuery(id+"F0.wireOp",EDGE,"E43");var subQ4=makeQuery(id+"F0.imprint","INTERSECT",VERTEX,{"derivedFrom":[subQ1,subQ3]});Q11=makeQuery(id+"F0.imprint","IMPRINT",FACE,{"disambiguationData":[TD([[makeQuery(id+"F0.imprint","IMPRINT",EDGE,{"disambiguationData":[TD([[subQ4,1.0]])],"derivedFrom":subQ3}),1.0]])]});}
            var Q12;
            {var subQ1=sQuery(id+"F0.wireOp",EDGE,"E14");var subQ3=sQuery(id+"F0.wireOp",EDGE,"E43");var subQ4=makeQuery(id+"F0.imprint","INTERSECT",VERTEX,{"derivedFrom":[subQ1,subQ3]});Q12=makeQuery(id+"F0.imprint","IMPRINT",FACE,{"disambiguationData":[TD([[makeQuery(id+"F0.imprint","IMPRINT",EDGE,{"disambiguationData":[TD([[subQ4,1.0]])],"derivedFrom":subQ3}),1.0]])]});}
            var Q13;
            {var subQ1=sQuery(id+"F0.wireOp",EDGE,"E15");var subQ3=sQuery(id+"F0.wireOp",EDGE,"E43");var subQ4=makeQuery(id+"F0.imprint","INTERSECT",VERTEX,{"derivedFrom":[subQ1,subQ3]});Q13=makeQuery(id+"F0.imprint","IMPRINT",FACE,{"disambiguationData":[TD([[makeQuery(id+"F0.imprint","IMPRINT",EDGE,{"disambiguationData":[TD([[subQ4,1.0]])],"derivedFrom":subQ3}),1.0]])]});}
            var Q14;
            {var subQ1=sQuery(id+"F0.wireOp",EDGE,"E16");var subQ3=sQuery(id+"F0.wireOp",EDGE,"E43");var subQ4=makeQuery(id+"F0.imprint","INTERSECT",VERTEX,{"derivedFrom":[subQ1,subQ3]});Q14=makeQuery(id+"F0.imprint","IMPRINT",FACE,{"disambiguationData":[TD([[makeQuery(id+"F0.imprint","IMPRINT",EDGE,{"disambiguationData":[TD([[subQ4,1.0]])],"derivedFrom":subQ3}),1.0]])]});}
            var Q15;
            {var subQ1=sQuery(id+"F0.wireOp",EDGE,"E17");var subQ3=sQuery(id+"F0.wireOp",EDGE,"E43");var subQ4=makeQuery(id+"F0.imprint","INTERSECT",VERTEX,{"derivedFrom":[subQ1,subQ3]});Q15=makeQuery(id+"F0.imprint","IMPRINT",FACE,{"disambiguationData":[TD([[makeQuery(id+"F0.imprint","IMPRINT",EDGE,{"disambiguationData":[TD([[subQ4,1.0]])],"derivedFrom":subQ3}),1.0]])]});}
            var Q16;
            {var subQ1=sQuery(id+"F0.wireOp",EDGE,"E18");var subQ3=sQuery(id+"F0.wireOp",EDGE,"E43");var subQ4=makeQuery(id+"F0.imprint","INTERSECT",VERTEX,{"derivedFrom":[subQ1,subQ3]});Q16=makeQuery(id+"F0.imprint","IMPRINT",FACE,{"disambiguationData":[TD([[makeQuery(id+"F0.imprint","IMPRINT",EDGE,{"disambiguationData":[TD([[subQ4,1.0]])],"derivedFrom":subQ3}),1.0]])]});}
            var Q17;
            {var subQ1=sQuery(id+"F0.wireOp",EDGE,"E19");var subQ3=sQuery(id+"F0.wireOp",EDGE,"E43");var subQ4=makeQuery(id+"F0.imprint","INTERSECT",VERTEX,{"derivedFrom":[subQ1,subQ3]});Q17=makeQuery(id+"F0.imprint","IMPRINT",FACE,{"disambiguationData":[TD([[makeQuery(id+"F0.imprint","IMPRINT",EDGE,{"disambiguationData":[TD([[subQ4,1.0]])],"derivedFrom":subQ3}),1.0]])]});}
            extrude(context, id + "F5", {"entities" : qUnion([Q0, Q1, Q2, Q3, Q4, Q5, Q6, Q7, Q8, Q9, Q10, Q11, Q12, Q13, Q14, Q15, Q16, Q17]), "operationType" : NewBodyOperationType.ADD, "depth" : 50.8 * mm, "offsetDistance" : 25.4 * mm});
        }
        {
            var Q0;
            {var subQ6=sQuery(id+"F0.wireOp",EDGE,"E1.13");Q0=makeQuery(id+"F0.imprint","IMPRINT",FACE,{"disambiguationData":[TD([[makeQuery(id+"F0.imprint","IMPRINT",EDGE,{"derivedFrom":subQ6}),-1.0]])]});}
            var Q1;
            {var subQ6=sQuery(id+"F0.wireOp",EDGE,"E1.19");Q1=makeQuery(id+"F0.imprint","IMPRINT",FACE,{"disambiguationData":[TD([[makeQuery(id+"F0.imprint","IMPRINT",EDGE,{"derivedFrom":subQ6}),-1.0]])]});}
            var Q2;
            {var subQ6=sQuery(id+"F0.wireOp",EDGE,"E1.25");Q2=makeQuery(id+"F0.imprint","IMPRINT",FACE,{"disambiguationData":[TD([[makeQuery(id+"F0.imprint","IMPRINT",EDGE,{"derivedFrom":subQ6}),-1.0]])]});}
            var Q3;
            {var subQ6=sQuery(id+"F0.wireOp",EDGE,"E1.31");Q3=makeQuery(id+"F0.imprint","IMPRINT",FACE,{"disambiguationData":[TD([[makeQuery(id+"F0.imprint","IMPRINT",EDGE,{"derivedFrom":subQ6}),-1.0]])]});}
            var Q4;
            {var subQ6=sQuery(id+"F0.wireOp",EDGE,"E1.37");Q4=makeQuery(id+"F0.imprint","IMPRINT",FACE,{"disambiguationData":[TD([[makeQuery(id+"F0.imprint","IMPRINT",EDGE,{"derivedFrom":subQ6}),-1.0]])]});}
            var Q5;
            {var subQ1=sQuery(id+"F0.wireOp",EDGE,"E8");var subQ3=sQuery(id+"F0.wireOp",EDGE,"E43");var subQ4=makeQuery(id+"F0.imprint","INTERSECT",VERTEX,{"derivedFrom":[subQ1,subQ3]});Q5=makeQuery(id+"F0.imprint","IMPRINT",FACE,{"disambiguationData":[TD([[makeQuery(id+"F0.imprint","IMPRINT",EDGE,{"disambiguationData":[TD([[subQ4,1.0]])],"derivedFrom":subQ3}),1.0]])]});}
            var Q6;
            {var subQ1=sQuery(id+"F0.wireOp",EDGE,"E9");var subQ3=sQuery(id+"F0.wireOp",EDGE,"E43");var subQ4=makeQuery(id+"F0.imprint","INTERSECT",VERTEX,{"derivedFrom":[subQ1,subQ3]});Q6=makeQuery(id+"F0.imprint","IMPRINT",FACE,{"disambiguationData":[TD([[makeQuery(id+"F0.imprint","IMPRINT",EDGE,{"disambiguationData":[TD([[subQ4,1.0]])],"derivedFrom":subQ3}),1.0]])]});}
            var Q7;
            {var subQ1=sQuery(id+"F0.wireOp",EDGE,"E10");var subQ3=sQuery(id+"F0.wireOp",EDGE,"E43");var subQ4=makeQuery(id+"F0.imprint","INTERSECT",VERTEX,{"derivedFrom":[subQ1,subQ3]});Q7=makeQuery(id+"F0.imprint","IMPRINT",FACE,{"disambiguationData":[TD([[makeQuery(id+"F0.imprint","IMPRINT",EDGE,{"disambiguationData":[TD([[subQ4,1.0]])],"derivedFrom":subQ3}),1.0]])]});}
            var Q8;
            {var subQ1=sQuery(id+"F0.wireOp",EDGE,"E11");var subQ3=sQuery(id+"F0.wireOp",EDGE,"E43");var subQ4=makeQuery(id+"F0.imprint","INTERSECT",VERTEX,{"derivedFrom":[subQ1,subQ3]});Q8=makeQuery(id+"F0.imprint","IMPRINT",FACE,{"disambiguationData":[TD([[makeQuery(id+"F0.imprint","IMPRINT",EDGE,{"disambiguationData":[TD([[subQ4,1.0]])],"derivedFrom":subQ3}),1.0]])]});}
            var Q9;
            {var subQ1=sQuery(id+"F0.wireOp",EDGE,"E12");var subQ3=sQuery(id+"F0.wireOp",EDGE,"E43");var subQ4=makeQuery(id+"F0.imprint","INTERSECT",VERTEX,{"derivedFrom":[subQ1,subQ3]});Q9=makeQuery(id+"F0.imprint","IMPRINT",FACE,{"disambiguationData":[TD([[makeQuery(id+"F0.imprint","IMPRINT",EDGE,{"disambiguationData":[TD([[subQ4,1.0]])],"derivedFrom":subQ3}),1.0]])]});}
            var Q10;
            {var subQ1=sQuery(id+"F0.wireOp",EDGE,"E13");var subQ3=sQuery(id+"F0.wireOp",EDGE,"E43");var subQ4=makeQuery(id+"F0.imprint","INTERSECT",VERTEX,{"derivedFrom":[subQ1,subQ3]});Q10=makeQuery(id+"F0.imprint","IMPRINT",FACE,{"disambiguationData":[TD([[makeQuery(id+"F0.imprint","IMPRINT",EDGE,{"disambiguationData":[TD([[subQ4,1.0]])],"derivedFrom":subQ3}),1.0]])]});}
            var Q11;
            {var subQ1=sQuery(id+"F0.wireOp",EDGE,"E14");var subQ3=sQuery(id+"F0.wireOp",EDGE,"E43");var subQ4=makeQuery(id+"F0.imprint","INTERSECT",VERTEX,{"derivedFrom":[subQ1,subQ3]});Q11=makeQuery(id+"F0.imprint","IMPRINT",FACE,{"disambiguationData":[TD([[makeQuery(id+"F0.imprint","IMPRINT",EDGE,{"disambiguationData":[TD([[subQ4,1.0]])],"derivedFrom":subQ3}),1.0]])]});}
            var Q12;
            {var subQ1=sQuery(id+"F0.wireOp",EDGE,"E15");var subQ3=sQuery(id+"F0.wireOp",EDGE,"E43");var subQ4=makeQuery(id+"F0.imprint","INTERSECT",VERTEX,{"derivedFrom":[subQ1,subQ3]});Q12=makeQuery(id+"F0.imprint","IMPRINT",FACE,{"disambiguationData":[TD([[makeQuery(id+"F0.imprint","IMPRINT",EDGE,{"disambiguationData":[TD([[subQ4,1.0]])],"derivedFrom":subQ3}),1.0]])]});}
            var Q13;
            {var subQ1=sQuery(id+"F0.wireOp",EDGE,"E16");var subQ3=sQuery(id+"F0.wireOp",EDGE,"E43");var subQ4=makeQuery(id+"F0.imprint","INTERSECT",VERTEX,{"derivedFrom":[subQ1,subQ3]});Q13=makeQuery(id+"F0.imprint","IMPRINT",FACE,{"disambiguationData":[TD([[makeQuery(id+"F0.imprint","IMPRINT",EDGE,{"disambiguationData":[TD([[subQ4,1.0]])],"derivedFrom":subQ3}),1.0]])]});}
            var Q14;
            {var subQ1=sQuery(id+"F0.wireOp",EDGE,"E17");var subQ3=sQuery(id+"F0.wireOp",EDGE,"E43");var subQ4=makeQuery(id+"F0.imprint","INTERSECT",VERTEX,{"derivedFrom":[subQ1,subQ3]});Q14=makeQuery(id+"F0.imprint","IMPRINT",FACE,{"disambiguationData":[TD([[makeQuery(id+"F0.imprint","IMPRINT",EDGE,{"disambiguationData":[TD([[subQ4,1.0]])],"derivedFrom":subQ3}),1.0]])]});}
            var Q15;
            {var subQ1=sQuery(id+"F0.wireOp",EDGE,"E18");var subQ3=sQuery(id+"F0.wireOp",EDGE,"E43");var subQ4=makeQuery(id+"F0.imprint","INTERSECT",VERTEX,{"derivedFrom":[subQ1,subQ3]});Q15=makeQuery(id+"F0.imprint","IMPRINT",FACE,{"disambiguationData":[TD([[makeQuery(id+"F0.imprint","IMPRINT",EDGE,{"disambiguationData":[TD([[subQ4,1.0]])],"derivedFrom":subQ3}),1.0]])]});}
            var Q16;
            {var subQ1=sQuery(id+"F0.wireOp",EDGE,"E19");var subQ3=sQuery(id+"F0.wireOp",EDGE,"E43");var subQ4=makeQuery(id+"F0.imprint","INTERSECT",VERTEX,{"derivedFrom":[subQ1,subQ3]});Q16=makeQuery(id+"F0.imprint","IMPRINT",FACE,{"disambiguationData":[TD([[makeQuery(id+"F0.imprint","IMPRINT",EDGE,{"disambiguationData":[TD([[subQ4,1.0]])],"derivedFrom":subQ3}),1.0]])]});}
            var Q17;
            {var subQ1=sQuery(id+"F0.wireOp",EDGE,"E6");var subQ3=sQuery(id+"F0.wireOp",EDGE,"E43");var subQ4=makeQuery(id+"F0.imprint","INTERSECT",VERTEX,{"derivedFrom":[subQ1,subQ3]});Q17=makeQuery(id+"F0.imprint","IMPRINT",FACE,{"disambiguationData":[TD([[makeQuery(id+"F0.imprint","IMPRINT",EDGE,{"disambiguationData":[TD([[subQ4,-1.0]])],"derivedFrom":subQ3}),1.0]])]});}
            extrude(context, id + "F6", {"entities" : qUnion([Q0, Q1, Q2, Q3, Q4, Q5, Q6, Q7, Q8, Q9, Q10, Q11, Q12, Q13, Q14, Q15, Q16, Q17]), "operationType" : NewBodyOperationType.ADD, "depth" : 63.5 * mm, "offsetDistance" : 25.4 * mm});
        }
        {
            var Q0;
            {var subQ1=sQuery(id+"F0.wireOp",EDGE,"E5");var subQ3=sQuery(id+"F0.wireOp",EDGE,"E43");var subQ4=makeQuery(id+"F0.imprint","INTERSECT",VERTEX,{"derivedFrom":[subQ1,subQ3]});Q0=makeQuery(id+"F0.imprint","IMPRINT",FACE,{"disambiguationData":[TD([[makeQuery(id+"F0.imprint","IMPRINT",EDGE,{"disambiguationData":[TD([[subQ4,-1.0]])],"derivedFrom":subQ3}),1.0]])]});}
            var Q1;
            {var subQ1=sQuery(id+"F0.wireOp",EDGE,"E6");var subQ3=sQuery(id+"F0.wireOp",EDGE,"E43");var subQ4=makeQuery(id+"F0.imprint","INTERSECT",VERTEX,{"derivedFrom":[subQ1,subQ3]});Q1=makeQuery(id+"F0.imprint","IMPRINT",FACE,{"disambiguationData":[TD([[makeQuery(id+"F0.imprint","IMPRINT",EDGE,{"disambiguationData":[TD([[subQ4,-1.0]])],"derivedFrom":subQ3}),1.0]])]});}
            var Q2;
            {var subQ1=sQuery(id+"F0.wireOp",EDGE,"E19");var subQ3=sQuery(id+"F0.wireOp",EDGE,"E43");var subQ4=makeQuery(id+"F0.imprint","INTERSECT",VERTEX,{"derivedFrom":[subQ1,subQ3]});Q2=makeQuery(id+"F0.imprint","IMPRINT",FACE,{"disambiguationData":[TD([[makeQuery(id+"F0.imprint","IMPRINT",EDGE,{"disambiguationData":[TD([[subQ4,1.0]])],"derivedFrom":subQ3}),1.0]])]});}
            var Q3;
            {var subQ1=sQuery(id+"F0.wireOp",EDGE,"E18");var subQ3=sQuery(id+"F0.wireOp",EDGE,"E43");var subQ4=makeQuery(id+"F0.imprint","INTERSECT",VERTEX,{"derivedFrom":[subQ1,subQ3]});Q3=makeQuery(id+"F0.imprint","IMPRINT",FACE,{"disambiguationData":[TD([[makeQuery(id+"F0.imprint","IMPRINT",EDGE,{"disambiguationData":[TD([[subQ4,1.0]])],"derivedFrom":subQ3}),1.0]])]});}
            var Q4;
            {var subQ1=sQuery(id+"F0.wireOp",EDGE,"E17");var subQ3=sQuery(id+"F0.wireOp",EDGE,"E43");var subQ4=makeQuery(id+"F0.imprint","INTERSECT",VERTEX,{"derivedFrom":[subQ1,subQ3]});Q4=makeQuery(id+"F0.imprint","IMPRINT",FACE,{"disambiguationData":[TD([[makeQuery(id+"F0.imprint","IMPRINT",EDGE,{"disambiguationData":[TD([[subQ4,1.0]])],"derivedFrom":subQ3}),1.0]])]});}
            var Q5;
            {var subQ1=sQuery(id+"F0.wireOp",EDGE,"E16");var subQ3=sQuery(id+"F0.wireOp",EDGE,"E43");var subQ4=makeQuery(id+"F0.imprint","INTERSECT",VERTEX,{"derivedFrom":[subQ1,subQ3]});Q5=makeQuery(id+"F0.imprint","IMPRINT",FACE,{"disambiguationData":[TD([[makeQuery(id+"F0.imprint","IMPRINT",EDGE,{"disambiguationData":[TD([[subQ4,1.0]])],"derivedFrom":subQ3}),1.0]])]});}
            var Q6;
            {var subQ1=sQuery(id+"F0.wireOp",EDGE,"E15");var subQ3=sQuery(id+"F0.wireOp",EDGE,"E43");var subQ4=makeQuery(id+"F0.imprint","INTERSECT",VERTEX,{"derivedFrom":[subQ1,subQ3]});Q6=makeQuery(id+"F0.imprint","IMPRINT",FACE,{"disambiguationData":[TD([[makeQuery(id+"F0.imprint","IMPRINT",EDGE,{"disambiguationData":[TD([[subQ4,1.0]])],"derivedFrom":subQ3}),1.0]])]});}
            var Q7;
            {var subQ1=sQuery(id+"F0.wireOp",EDGE,"E14");var subQ3=sQuery(id+"F0.wireOp",EDGE,"E43");var subQ4=makeQuery(id+"F0.imprint","INTERSECT",VERTEX,{"derivedFrom":[subQ1,subQ3]});Q7=makeQuery(id+"F0.imprint","IMPRINT",FACE,{"disambiguationData":[TD([[makeQuery(id+"F0.imprint","IMPRINT",EDGE,{"disambiguationData":[TD([[subQ4,1.0]])],"derivedFrom":subQ3}),1.0]])]});}
            var Q8;
            {var subQ1=sQuery(id+"F0.wireOp",EDGE,"E13");var subQ3=sQuery(id+"F0.wireOp",EDGE,"E43");var subQ4=makeQuery(id+"F0.imprint","INTERSECT",VERTEX,{"derivedFrom":[subQ1,subQ3]});Q8=makeQuery(id+"F0.imprint","IMPRINT",FACE,{"disambiguationData":[TD([[makeQuery(id+"F0.imprint","IMPRINT",EDGE,{"disambiguationData":[TD([[subQ4,1.0]])],"derivedFrom":subQ3}),1.0]])]});}
            var Q9;
            {var subQ1=sQuery(id+"F0.wireOp",EDGE,"E12");var subQ3=sQuery(id+"F0.wireOp",EDGE,"E43");var subQ4=makeQuery(id+"F0.imprint","INTERSECT",VERTEX,{"derivedFrom":[subQ1,subQ3]});Q9=makeQuery(id+"F0.imprint","IMPRINT",FACE,{"disambiguationData":[TD([[makeQuery(id+"F0.imprint","IMPRINT",EDGE,{"disambiguationData":[TD([[subQ4,1.0]])],"derivedFrom":subQ3}),1.0]])]});}
            var Q10;
            {var subQ1=sQuery(id+"F0.wireOp",EDGE,"E11");var subQ3=sQuery(id+"F0.wireOp",EDGE,"E43");var subQ4=makeQuery(id+"F0.imprint","INTERSECT",VERTEX,{"derivedFrom":[subQ1,subQ3]});Q10=makeQuery(id+"F0.imprint","IMPRINT",FACE,{"disambiguationData":[TD([[makeQuery(id+"F0.imprint","IMPRINT",EDGE,{"disambiguationData":[TD([[subQ4,1.0]])],"derivedFrom":subQ3}),1.0]])]});}
            var Q11;
            {var subQ1=sQuery(id+"F0.wireOp",EDGE,"E10");var subQ3=sQuery(id+"F0.wireOp",EDGE,"E43");var subQ4=makeQuery(id+"F0.imprint","INTERSECT",VERTEX,{"derivedFrom":[subQ1,subQ3]});Q11=makeQuery(id+"F0.imprint","IMPRINT",FACE,{"disambiguationData":[TD([[makeQuery(id+"F0.imprint","IMPRINT",EDGE,{"disambiguationData":[TD([[subQ4,1.0]])],"derivedFrom":subQ3}),1.0]])]});}
            var Q12;
            {var subQ1=sQuery(id+"F0.wireOp",EDGE,"E9");var subQ3=sQuery(id+"F0.wireOp",EDGE,"E43");var subQ4=makeQuery(id+"F0.imprint","INTERSECT",VERTEX,{"derivedFrom":[subQ1,subQ3]});Q12=makeQuery(id+"F0.imprint","IMPRINT",FACE,{"disambiguationData":[TD([[makeQuery(id+"F0.imprint","IMPRINT",EDGE,{"disambiguationData":[TD([[subQ4,1.0]])],"derivedFrom":subQ3}),1.0]])]});}
            var Q13;
            {var subQ1=sQuery(id+"F0.wireOp",EDGE,"E8");var subQ3=sQuery(id+"F0.wireOp",EDGE,"E43");var subQ4=makeQuery(id+"F0.imprint","INTERSECT",VERTEX,{"derivedFrom":[subQ1,subQ3]});Q13=makeQuery(id+"F0.imprint","IMPRINT",FACE,{"disambiguationData":[TD([[makeQuery(id+"F0.imprint","IMPRINT",EDGE,{"disambiguationData":[TD([[subQ4,1.0]])],"derivedFrom":subQ3}),1.0]])]});}
            var Q14;
            {var subQ1=sQuery(id+"F0.wireOp",EDGE,"E7");var subQ3=sQuery(id+"F0.wireOp",EDGE,"E43");var subQ4=makeQuery(id+"F0.imprint","INTERSECT",VERTEX,{"derivedFrom":[subQ1,subQ3]});Q14=makeQuery(id+"F0.imprint","IMPRINT",FACE,{"disambiguationData":[TD([[makeQuery(id+"F0.imprint","IMPRINT",EDGE,{"disambiguationData":[TD([[subQ4,1.0]])],"derivedFrom":subQ3}),1.0]])]});}
            var Q15;
            {var subQ1=sQuery(id+"F0.wireOp",EDGE,"E4");var subQ3=sQuery(id+"F0.wireOp",EDGE,"E43");var subQ4=makeQuery(id+"F0.imprint","INTERSECT",VERTEX,{"derivedFrom":[subQ1,subQ3]});Q15=makeQuery(id+"F0.imprint","IMPRINT",FACE,{"disambiguationData":[TD([[makeQuery(id+"F0.imprint","IMPRINT",EDGE,{"disambiguationData":[TD([[subQ4,1.0]])],"derivedFrom":subQ3}),1.0]])]});}
            var Q16;
            {var subQ1=sQuery(id+"F0.wireOp",EDGE,"E3");var subQ3=sQuery(id+"F0.wireOp",EDGE,"E43");var subQ4=makeQuery(id+"F0.imprint","INTERSECT",VERTEX,{"derivedFrom":[subQ1,subQ3]});Q16=makeQuery(id+"F0.imprint","IMPRINT",FACE,{"disambiguationData":[TD([[makeQuery(id+"F0.imprint","IMPRINT",EDGE,{"disambiguationData":[TD([[subQ4,1.0]])],"derivedFrom":subQ3}),1.0]])]});}
            var Q17;
            {var subQ1=sQuery(id+"F0.wireOp",EDGE,"E2");var subQ3=sQuery(id+"F0.wireOp",EDGE,"E43");var subQ4=makeQuery(id+"F0.imprint","INTERSECT",VERTEX,{"derivedFrom":[subQ1,subQ3]});Q17=makeQuery(id+"F0.imprint","IMPRINT",FACE,{"disambiguationData":[TD([[makeQuery(id+"F0.imprint","IMPRINT",EDGE,{"disambiguationData":[TD([[subQ4,1.0]])],"derivedFrom":subQ3}),1.0]])]});}
            var Q18;
            {var subQ1=sQuery(id+"F0.wireOp",EDGE,"E2");var subQ3=sQuery(id+"F0.wireOp",EDGE,"E43");var subQ4=makeQuery(id+"F0.imprint","INTERSECT",VERTEX,{"derivedFrom":[subQ1,subQ3]});Q18=makeQuery(id+"F0.imprint","IMPRINT",FACE,{"disambiguationData":[TD([[makeQuery(id+"F0.imprint","IMPRINT",EDGE,{"disambiguationData":[TD([[subQ4,-1.0]])],"derivedFrom":subQ3}),1.0]])]});}
            extrude(context, id + "F7", {"entities" : qUnion([Q0, Q1, Q2, Q3, Q4, Q5, Q6, Q7, Q8, Q9, Q10, Q11, Q12, Q13, Q14, Q15, Q16, Q17, Q18]), "operationType" : NewBodyOperationType.ADD, "depth" : 76.2 * mm, "offsetDistance" : 25.4 * mm});
        }
    });
